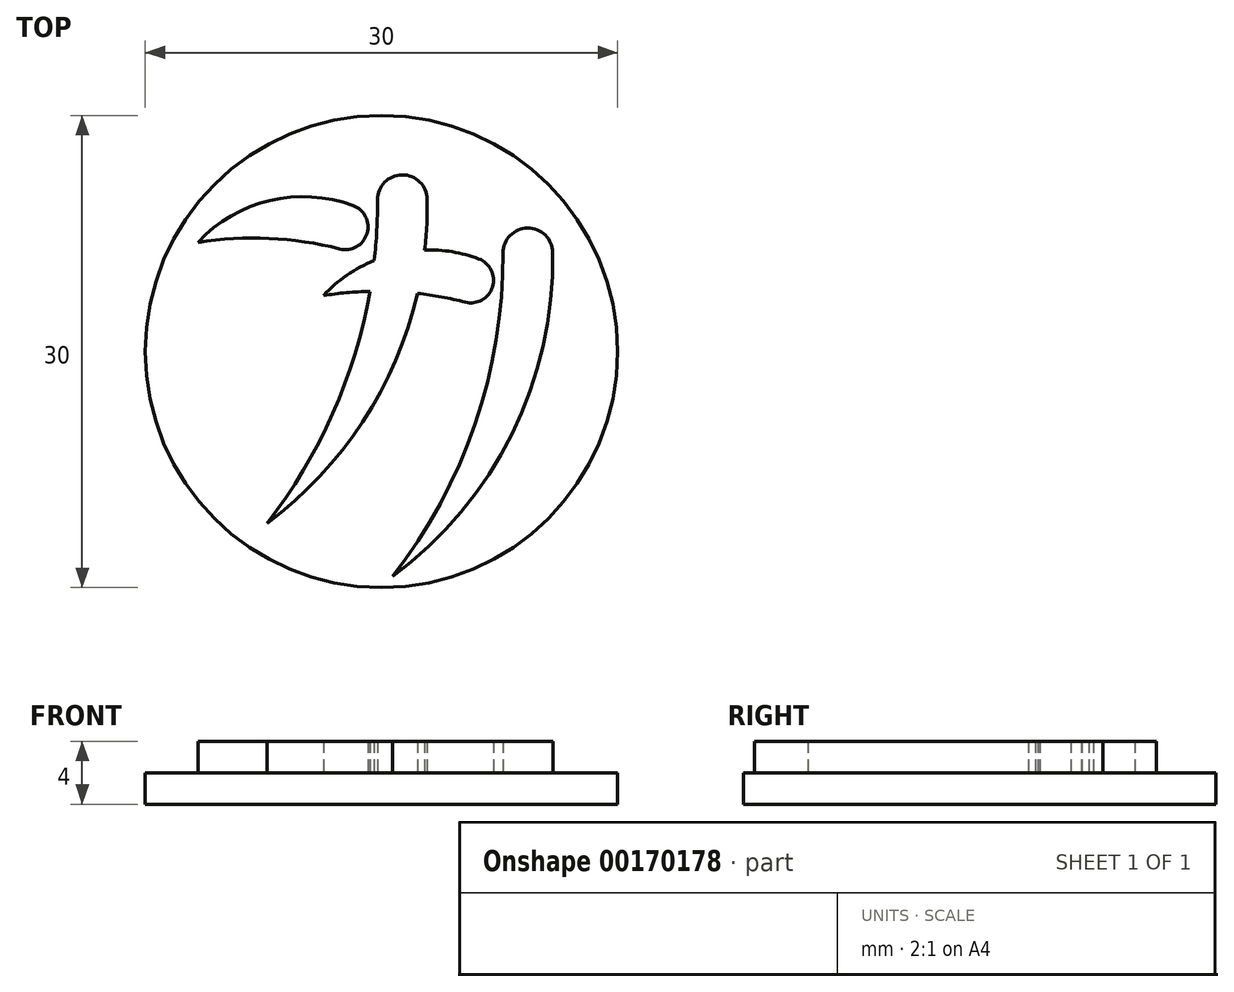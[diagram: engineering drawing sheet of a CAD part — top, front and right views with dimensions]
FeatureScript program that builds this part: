
annotation { "Feature Type Name" : "Feature", "Feature Type Description" : "" }
export const myFeature = defineFeature(function(context is Context, id is Id, definition is map)
    precondition{}
    {
        {
            var Q0;
            Q0=qCreatedBy(makeId("Top.planeOp"),FACE);
            var sketch = newSketch(context, id + "F0", { "sketchPlane" : qUnion([Q0])});
            skCircle(sketch, "E0", {"center": v(0, 0) * mm, "radius": 15 * mm});
            skSolve(sketch);
        }
        {
            var Q0;
            Q0 = qSketchRegion(id + "F0", true);
            extrude(context, id + "F1", {"entities" : qUnion([Q0]), "depth" : 2 * mm});
        }
        {
            var Q0;
            Q0=makeQuery(id+"F1.opExtrude","CAP_FACE",FACE,{"disambiguationData":[OSD([sQuery(id+"F0.wireOp",EDGE,"E0")])],"isStart":false});
            var sketch = newSketch(context, id + "F2", { "sketchPlane" : qUnion([Q0])});
            skArc(sketch, "E1", {"start": v(-2.65, 6.52) * mm, "mid": v(-0.92, 7.49) * mm, "end": v(-1.8, 9.27) * mm});
            skArc(sketch, "E2", {"start": v(-2.65, 6.52) * mm, "mid": v(-7.13, 7.19) * mm, "end": v(-11.66, 6.94) * mm});
            skArc(sketch, "E3", {"start": v(-1.8, 9.27) * mm, "mid": v(-7.08, 9.6) * mm, "end": v(-11.66, 6.94) * mm});
            skArc(sketch, "E4", {"start": v(2.9, 9.67) * mm, "mid": v(1.31, 11.22) * mm, "end": v(-0.25, 9.63) * mm});
            skArc(sketch, "E5", {"start": v(-7.27, -10.91) * mm, "mid": v(-3.1, -3.95) * mm, "end": v(-0.74, 3.82) * mm});
            skArc(sketch, "E6", {"start": v(-7.27, -10.91) * mm, "mid": v(-1.19, -4.47) * mm, "end": v(2.28, 3.69) * mm});
            skArc(sketch, "E7", {"start": v(5.32, 3.14) * mm, "mid": v(7.06, 4.1) * mm, "end": v(6.18, 5.89) * mm});
            skArc(sketch, "E8", {"start": v(5.32, 3.14) * mm, "mid": v(3.81, 3.47) * mm, "end": v(2.28, 3.69) * mm});
            skArc(sketch, "E9", {"start": v(6.18, 5.89) * mm, "mid": v(4.5, 6.34) * mm, "end": v(2.75, 6.46) * mm});
            skArc(sketch, "E10", {"start": v(10.88, 6.28) * mm, "mid": v(9.29, 7.84) * mm, "end": v(7.73, 6.25) * mm});
            skArc(sketch, "E11", {"start": v(0.7, -14.3) * mm, "mid": v(5.95, -4.61) * mm, "end": v(7.73, 6.25) * mm});
            skArc(sketch, "E12", {"start": v(0.7, -14.3) * mm, "mid": v(8.28, -5.24) * mm, "end": v(10.88, 6.28) * mm});
            skArc(sketch, "E13.trimOffspring", {"start": v(-0.46, 5.78) * mm, "mid": v(-0.3, 7.7) * mm, "end": v(-0.25, 9.63) * mm});
            skArc(sketch, "E14.trimOffspring", {"start": v(2.75, 6.46) * mm, "mid": v(2.88, 8.06) * mm, "end": v(2.9, 9.67) * mm});
            skArc(sketch, "E15.trimOffspring", {"start": v(-0.46, 5.78) * mm, "mid": v(-2.2, 4.84) * mm, "end": v(-3.68, 3.55) * mm});
            skArc(sketch, "E16.trimOffspring", {"start": v(-0.74, 3.82) * mm, "mid": v(-2.21, 3.74) * mm, "end": v(-3.68, 3.55) * mm});
            skSolve(sketch);
        }
        {
            var Q0;
            Q0 = qSketchRegion(id + "F2", true);
            extrude(context, id + "F3", {"entities" : qUnion([Q0]), "operationType" : NewBodyOperationType.ADD, "depth" : 2 * mm});
        }
    });
